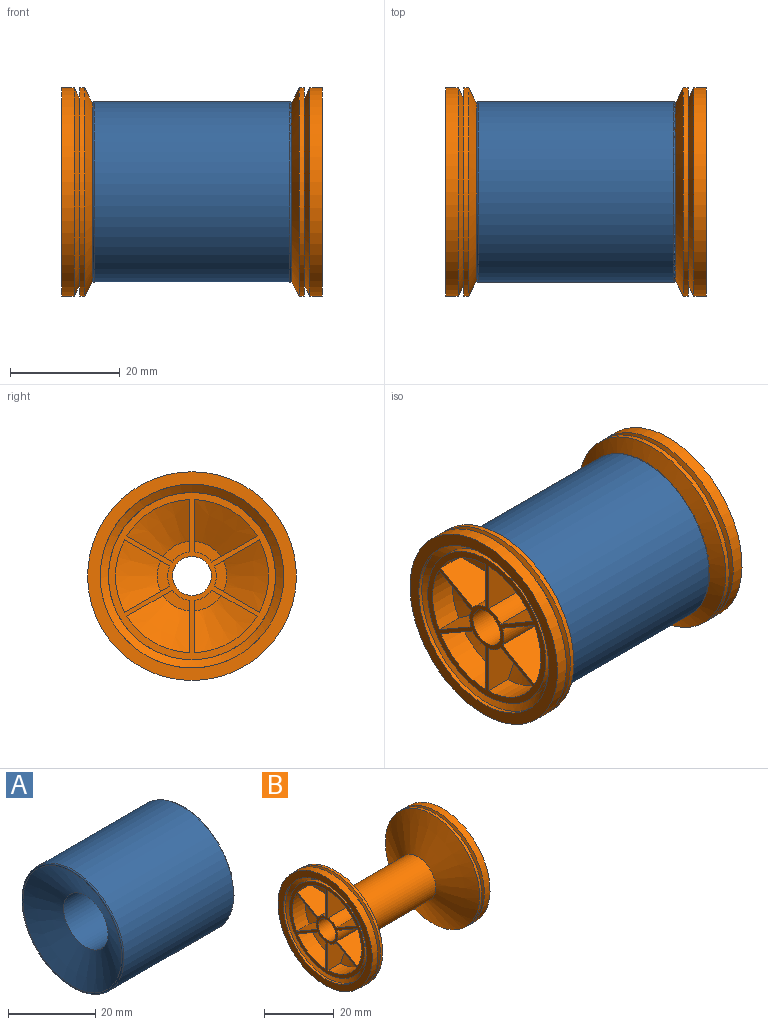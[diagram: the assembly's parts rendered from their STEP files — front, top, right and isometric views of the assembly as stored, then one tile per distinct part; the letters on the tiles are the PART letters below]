
ASSEMBLY  parts=2 mates=1
PART A: 6 faces, bbox 36.3x35.7x35.7 mm
  f0: cone r=7.24mm half-angle=63.5deg, axis (-1,0,0), area 720.4mm2, adj f1,f5
  f1: cylinder r=7.24mm len=27.43mm, axis (1,0,0), area 1247.7mm2, adj f0,f2
  f2: cone r=16.51mm half-angle=63.5deg, axis (1,0,0), area 720.4mm2, adj f1,f4
  f3: cylinder r=16.51mm len=35.65mm, axis (1,0,0), area 3698.2mm2, adj f4,f5
  f4: torus R=16.19mm, axis (-1,0,0), area 66.2mm2, adj f2,f3
  f5: torus R=16.19mm, axis (-1,0,0), area 66.2mm2, adj f0,f3
PART B: 108 faces, bbox 47.8x38.2x38.2 mm
  f0: cylinder r=19.05mm len=38.1mm, axis (-1,0,0), area 273.6mm2, adj f4,f102
  f1: cylinder r=19.05mm len=38.1mm, axis (-1,0,0), area 273.6mm2, adj f5,f98
  f2: cylinder r=3.56mm len=46.1mm, axis (-1,0,0), area 1030mm2, adj f3,f52
  f3: plane 30.48x30.48mm, normal (1,0,0), area 185.4mm2, adj f2,f7,f8,f9,f10,f11,f12,f13
  f4: plane 38.1x38.1mm, normal (1,0,0), area 257.2mm2, adj f0,f6
  f5: plane 38.1x38.1mm, normal (-1,0,0), area 257.2mm2, adj f1,f51
  f6: cylinder r=16.76mm len=33.53mm, axis (1,0,0), area 80.3mm2, adj f4,f32
  f7: cylinder r=4.45mm len=22.61mm, axis (1,0,0), area 86.8mm2, adj f3,f8,f10,f44
  f8: plane 22.74x9.67mm, normal (0,-1,0), area 96.5mm2, adj f3,f7,f9,f43,f44,f50
  f9: cylinder r=13.97mm len=11.48mm, axis (1,0,0), area 70.2mm2, adj f3,f8,f10,f50
  f10: plane 22.74x8.39mm, normal (0,0.5,0.87), area 96.5mm2, adj f3,f7,f9,f43,f44,f50
  f11: cylinder r=4.45mm len=22.61mm, axis (1,0,0), area 86.8mm2, adj f3,f12,f14,f42
  f12: plane 22.74x8.39mm, normal (0,-0.5,0.87), area 96.5mm2, adj f3,f11,f13,f41,f42,f49
  f13: cylinder r=13.97mm len=11.48mm, axis (1,0,0), area 70.2mm2, adj f3,f12,f14,f49
  f14: plane 22.74x9.67mm, normal (0,1,0), area 96.5mm2, adj f3,f11,f13,f41,f42,f49
  f15: cylinder r=4.45mm len=22.61mm, axis (1,0,0), area 86.8mm2, adj f3,f16,f18,f40
  f16: plane 22.74x9.67mm, normal (0,1,0), area 96.5mm2, adj f3,f15,f17,f39,f40,f47
  f17: cylinder r=13.97mm len=11.48mm, axis (1,0,0), area 70.2mm2, adj f3,f16,f18,f47
  f18: plane 22.74x8.39mm, normal (0,-0.5,-0.87), area 96.5mm2, adj f3,f15,f17,f39,f40,f47
  f19: cylinder r=4.45mm len=22.61mm, axis (1,0,0), area 86.8mm2, adj f3,f20,f22,f38
  f20: plane 22.74x8.39mm, normal (0,0.5,0.87), area 96.5mm2, adj f3,f19,f21,f37,f38,f48
  f21: cylinder r=13.97mm len=13.26mm, axis (1,0,0), area 70.2mm2, adj f3,f20,f22,f48
  f22: plane 22.74x8.39mm, normal (0,0.5,-0.87), area 96.5mm2, adj f3,f19,f21,f37,f38,f48
  f23: cylinder r=4.45mm len=22.61mm, axis (1,0,0), area 86.8mm2, adj f3,f24,f26,f36
  f24: plane 22.74x8.39mm, normal (0,-0.5,-0.87), area 96.5mm2, adj f3,f23,f25,f35,f36,f45
  f25: cylinder r=13.97mm len=13.26mm, axis (1,0,0), area 70.2mm2, adj f3,f24,f26,f45
  f26: plane 22.74x8.39mm, normal (0,-0.5,0.87), area 96.5mm2, adj f3,f23,f25,f35,f36,f45
  f27: cylinder r=4.45mm len=22.61mm, axis (1,0,0), area 86.8mm2, adj f3,f28,f30,f34
  f28: plane 22.74x8.39mm, normal (0,0.5,-0.87), area 96.5mm2, adj f3,f27,f29,f33,f34,f46
  f29: cylinder r=13.97mm len=11.48mm, axis (1,0,0), area 70.2mm2, adj f3,f28,f30,f46
  f30: plane 22.74x9.67mm, normal (0,-1,0), area 96.5mm2, adj f3,f27,f29,f33,f34,f46
  f31: cylinder r=15.24mm len=30.48mm, axis (1,0,0), area 121.6mm2, adj f3,f32
  f32: cone r=15.24mm half-angle=50.2deg, axis (1,0,0), area 199.5mm2, adj f6,f31
  f33: cylinder r=6.35mm len=13.72mm, axis (1,0,0), area 80.1mm2, adj f28,f30,f34,f46
  f34: plane 4.88x3.77mm, normal (1,0,0), area 9.2mm2, adj f27,f28,f30,f33
  f35: cylinder r=6.35mm len=13.72mm, axis (1,0,0), area 80.1mm2, adj f24,f26,f36,f45
  f36: plane 5.63x2.31mm, normal (1,0,0), area 9.2mm2, adj f23,f24,f26,f35
  f37: cylinder r=6.35mm len=13.72mm, axis (1,0,0), area 80.1mm2, adj f20,f22,f38,f48
  f38: plane 5.63x2.31mm, normal (1,0,0), area 9.2mm2, adj f19,f20,f22,f37
  f39: cylinder r=6.35mm len=13.72mm, axis (1,0,0), area 80.1mm2, adj f16,f18,f40,f47
  f40: plane 4.88x3.77mm, normal (1,0,0), area 9.2mm2, adj f15,f16,f18,f39
  f41: cylinder r=6.35mm len=13.72mm, axis (1,0,0), area 80.1mm2, adj f12,f14,f42,f49
  f42: plane 4.88x3.77mm, normal (1,0,0), area 9.2mm2, adj f11,f12,f14,f41
  f43: cylinder r=6.35mm len=13.72mm, axis (1,0,0), area 80.1mm2, adj f8,f10,f44,f50
  f44: plane 4.88x3.77mm, normal (1,0,0), area 9.2mm2, adj f7,f8,f10,f43
  f45: cone r=6.35mm half-angle=63.4deg, axis (1,0,0), area 83mm2, adj f24,f25,f26,f35
  f46: cone r=6.35mm half-angle=63.4deg, axis (1,0,0), area 83mm2, adj f28,f29,f30,f33
  f47: cone r=6.35mm half-angle=63.4deg, axis (1,0,0), area 83mm2, adj f16,f17,f18,f39
  f48: cone r=6.35mm half-angle=63.4deg, axis (1,0,0), area 83mm2, adj f20,f21,f22,f37
  f49: cone r=6.35mm half-angle=63.4deg, axis (1,0,0), area 83mm2, adj f12,f13,f14,f41
  f50: cone r=6.35mm half-angle=63.4deg, axis (1,0,0), area 83mm2, adj f8,f9,f10,f43
  f51: cylinder r=16.76mm len=33.53mm, axis (-1,0,0), area 80.3mm2, adj f5,f78
  f52: plane 30.48x30.48mm, normal (-1,0,0), area 185.4mm2, adj f2,f53,f54,f55,f56,f57,f58,f59
  f53: cylinder r=4.45mm len=22.61mm, axis (-1,0,0), area 86.8mm2, adj f52,f54,f56,f90
  f54: plane 22.74x8.39mm, normal (0,0.5,0.87), area 96.5mm2, adj f52,f53,f55,f89,f90,f96
  f55: cylinder r=13.97mm len=11.48mm, axis (-1,0,0), area 70.2mm2, adj f52,f54,f56,f96
  f56: plane 22.74x9.67mm, normal (0,-1,0), area 96.5mm2, adj f52,f53,f55,f89,f90,f96
  f57: cylinder r=4.45mm len=22.61mm, axis (-1,0,0), area 86.8mm2, adj f52,f58,f60,f88
  f58: plane 22.74x9.67mm, normal (0,1,0), area 96.5mm2, adj f52,f57,f59,f87,f88,f95
  f59: cylinder r=13.97mm len=11.48mm, axis (-1,0,0), area 70.2mm2, adj f52,f58,f60,f95
  f60: plane 22.74x8.39mm, normal (0,-0.5,0.87), area 96.5mm2, adj f52,f57,f59,f87,f88,f95
  f61: cylinder r=4.45mm len=22.61mm, axis (-1,0,0), area 86.8mm2, adj f52,f62,f64,f86
  f62: plane 22.74x8.39mm, normal (0,-0.5,-0.87), area 96.5mm2, adj f52,f61,f63,f85,f86,f93
  f63: cylinder r=13.97mm len=11.48mm, axis (-1,0,0), area 70.2mm2, adj f52,f62,f64,f93
  f64: plane 22.74x9.67mm, normal (0,1,0), area 96.5mm2, adj f52,f61,f63,f85,f86,f93
  f65: cylinder r=4.45mm len=22.61mm, axis (-1,0,0), area 86.8mm2, adj f52,f66,f68,f84
  f66: plane 22.74x8.39mm, normal (0,0.5,-0.87), area 96.5mm2, adj f52,f65,f67,f83,f84,f94
  f67: cylinder r=13.97mm len=13.26mm, axis (-1,0,0), area 70.2mm2, adj f52,f66,f68,f94
  f68: plane 22.74x8.39mm, normal (0,0.5,0.87), area 96.5mm2, adj f52,f65,f67,f83,f84,f94
  f69: cylinder r=4.45mm len=22.61mm, axis (-1,0,0), area 86.8mm2, adj f52,f70,f72,f82
  f70: plane 22.74x8.39mm, normal (0,-0.5,0.87), area 96.5mm2, adj f52,f69,f71,f81,f82,f91
  f71: cylinder r=13.97mm len=13.26mm, axis (-1,0,0), area 70.2mm2, adj f52,f70,f72,f91
  f72: plane 22.74x8.39mm, normal (0,-0.5,-0.87), area 96.5mm2, adj f52,f69,f71,f81,f82,f91
  f73: cylinder r=4.45mm len=22.61mm, axis (-1,0,0), area 86.8mm2, adj f52,f74,f76,f80
  f74: plane 22.74x9.67mm, normal (0,-1,0), area 96.5mm2, adj f52,f73,f75,f79,f80,f92
  f75: cylinder r=13.97mm len=11.48mm, axis (-1,0,0), area 70.2mm2, adj f52,f74,f76,f92
  f76: plane 22.74x8.39mm, normal (0,0.5,-0.87), area 96.5mm2, adj f52,f73,f75,f79,f80,f92
  f77: cylinder r=15.24mm len=30.48mm, axis (-1,0,0), area 121.6mm2, adj f52,f78
  f78: cone r=16.76mm half-angle=50.2deg, axis (-1,0,0), area 199.5mm2, adj f51,f77
  f79: cylinder r=6.35mm len=13.72mm, axis (-1,0,0), area 80.1mm2, adj f74,f76,f80,f92
  f80: plane 4.88x3.77mm, normal (-1,0,0), area 9.2mm2, adj f73,f74,f76,f79
  f81: cylinder r=6.35mm len=13.72mm, axis (-1,0,0), area 80.1mm2, adj f70,f72,f82,f91
  f82: plane 5.63x2.31mm, normal (-1,0,0), area 9.2mm2, adj f69,f70,f72,f81
  f83: cylinder r=6.35mm len=13.72mm, axis (-1,0,0), area 80.1mm2, adj f66,f68,f84,f94
  f84: plane 5.63x2.31mm, normal (-1,0,0), area 9.2mm2, adj f65,f66,f68,f83
  f85: cylinder r=6.35mm len=13.72mm, axis (-1,0,0), area 80.1mm2, adj f62,f64,f86,f93
  f86: plane 4.88x3.77mm, normal (-1,0,0), area 9.2mm2, adj f61,f62,f64,f85
  f87: cylinder r=6.35mm len=13.72mm, axis (-1,0,0), area 80.1mm2, adj f58,f60,f88,f95
  f88: plane 4.88x3.77mm, normal (-1,0,0), area 9.2mm2, adj f57,f58,f60,f87
  f89: cylinder r=6.35mm len=13.72mm, axis (-1,0,0), area 80.1mm2, adj f54,f56,f90,f96
  f90: plane 4.88x3.77mm, normal (-1,0,0), area 9.2mm2, adj f53,f54,f56,f89
  f91: cone r=13.97mm half-angle=63.4deg, axis (-1,0,0), area 83mm2, adj f70,f71,f72,f81
  f92: cone r=13.97mm half-angle=63.4deg, axis (-1,0,0), area 83mm2, adj f74,f75,f76,f79
  f93: cone r=13.97mm half-angle=63.4deg, axis (-1,0,0), area 83mm2, adj f62,f63,f64,f85
  f94: cone r=13.97mm half-angle=63.4deg, axis (-1,0,0), area 83mm2, adj f66,f67,f68,f83
  f95: cone r=13.97mm half-angle=63.4deg, axis (-1,0,0), area 83mm2, adj f58,f59,f60,f87
  f96: cone r=13.97mm half-angle=63.4deg, axis (-1,0,0), area 83mm2, adj f54,f55,f56,f89
  f97: cone r=19.05mm half-angle=63.5deg, axis (-1,0,0), area 498.9mm2, adj f99,f103
  f98: cone r=14.86mm half-angle=63.5deg, axis (-1,0,0), area 498.9mm2, adj f1,f99
  f99: cylinder r=14.86mm len=29.72mm, axis (-1,0,0), area 96.4mm2, adj f97,f98
  f100: cone r=19.05mm half-angle=63.5deg, axis (1,0,0), area 498.9mm2, adj f101,f107
  f101: cylinder r=14.86mm len=29.72mm, axis (-1,0,0), area 96.4mm2, adj f100,f102
  f102: cone r=14.86mm half-angle=63.5deg, axis (1,0,0), area 498.9mm2, adj f0,f101
  f103: cylinder r=19.05mm len=38.1mm, axis (-1,0,0), area 106.4mm2, adj f97,f104
  f104: cone r=19.05mm half-angle=63.5deg, axis (-1,0,0), area 1090mm2, adj f103,f105
  f105: cylinder r=7.24mm len=27.43mm, axis (-1,0,0), area 1247.7mm2, adj f104,f106
  f106: cone r=19.05mm half-angle=63.5deg, axis (1,0,0), area 1090mm2, adj f105,f107
  f107: cylinder r=19.05mm len=38.1mm, axis (-1,0,0), area 106.4mm2, adj f100,f106
PLACE A at identity
PLACE B at identity
MATE fastened A.f0 <-> B.f0  axis (1,0,0) through (0,0,0)mm
